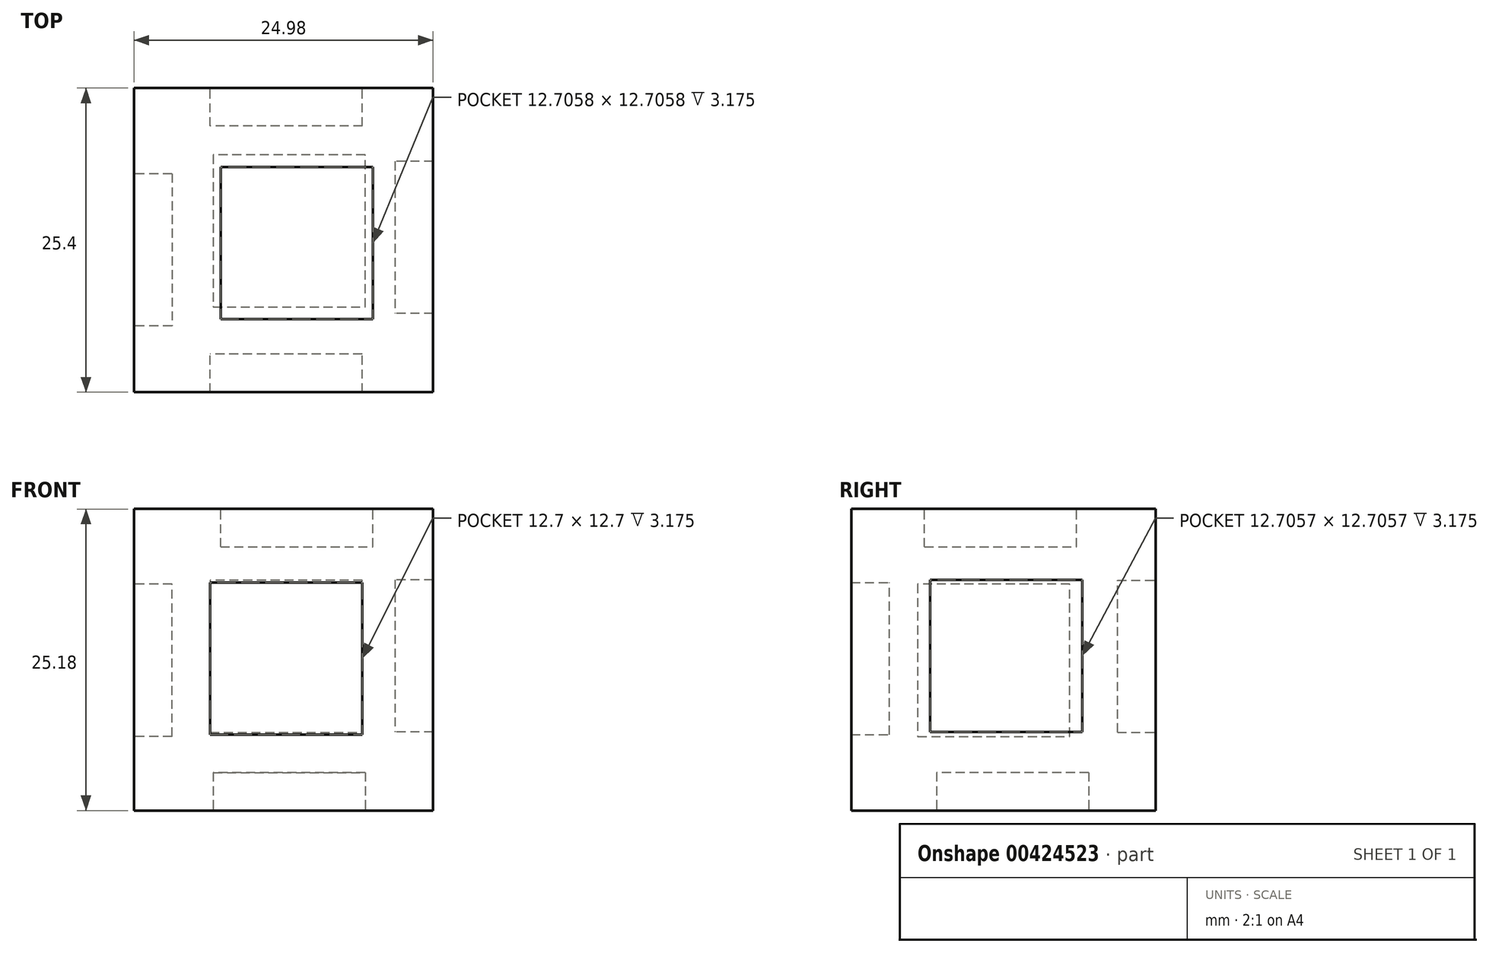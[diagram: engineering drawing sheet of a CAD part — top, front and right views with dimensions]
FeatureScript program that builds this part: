
annotation { "Feature Type Name" : "Feature", "Feature Type Description" : "" }
export const myFeature = defineFeature(function(context is Context, id is Id, definition is map)
    precondition{}
    {
        {
            var Q0;
            Q0=qCreatedBy(makeId("Front.planeOp"),FACE);
            var sketch = newSketch(context, id + "F0", { "sketchPlane" : qUnion([Q0])});
            skLineSegment(sketch, "E0", {"start": v(11.49, 11.84) * mm, "end": v(11.49, -13.56) * mm});
            skLineSegment(sketch, "E1", {"start": v(11.49, -13.56) * mm, "end": v(-13.49, -13.56) * mm});
            skLineSegment(sketch, "E2", {"start": v(-13.49, -13.56) * mm, "end": v(-13.49, 11.62) * mm});
            skLineSegment(sketch, "E3", {"start": v(-13.49, 11.62) * mm, "end": v(11.91, 11.62) * mm});
            skSolve(sketch);
        }
        {
            var Q0;
            Q0 = qSketchRegion(id + "F0", true);
            extrude(context, id + "F1", {"entities" : qUnion([Q0]), "depth" : 25.4 * mm});
        }
        {
            var Q0;
            Q0=makeQuery(id+"F1.opExtrude","CAP_FACE",FACE,{"disambiguationData":[OSD([sQuery(id+"F0.wireOp",EDGE,"E0"),sQuery(id+"F0.wireOp",EDGE,"E1"),sQuery(id+"F0.wireOp",EDGE,"E2"),sQuery(id+"F0.wireOp",EDGE,"E3")])],"isStart":false});
            var sketch = newSketch(context, id + "F2", { "sketchPlane" : qUnion([Q0])});
            skLineSegment(sketch, "E4", {"start": v(-7.14, 5.49) * mm, "end": v(5.56, 5.49) * mm});
            skLineSegment(sketch, "E5", {"start": v(5.56, 5.49) * mm, "end": v(5.56, -7.21) * mm});
            skLineSegment(sketch, "E6", {"start": v(5.56, -7.21) * mm, "end": v(-7.14, -7.21) * mm});
            skLineSegment(sketch, "E7", {"start": v(-7.14, -7.21) * mm, "end": v(-7.14, 5.49) * mm});
            skLineSegment(sketch, "E8", {"start": v(-7.14, 0) * mm, "end": v(-13.49, 0) * mm});
            skSolve(sketch);
        }
        {
            var Q0;
            {var subQ3=sQuery(id+"F2.wireOp",EDGE,"E4");Q0=makeQuery(id+"F2.imprint","IMPRINT",FACE,{"disambiguationData":[TD([[makeQuery(id+"F2.imprint","IMPRINT",EDGE,{"derivedFrom":subQ3}),-1.0]])]});}
            extrude(context, id + "F3", {"entities" : qUnion([Q0]), "operationType" : NewBodyOperationType.REMOVE, "oppositeDirection" : true, "depth" : 3.17 * mm});
        }
        {
            var Q0;
            Q0=makeQuery(id+"F1.opExtrude","SWEPT_FACE",FACE,{"disambiguationData":[OSD([sQuery(id+"F0.wireOp",EDGE,"E0")])]});
            var sketch = newSketch(context, id + "F4", { "sketchPlane" : qUnion([Q0])});
            skLineSegment(sketch, "E9", {"start": v(-6.12, 5.71) * mm, "end": v(-6.12, -7) * mm});
            skLineSegment(sketch, "E10", {"start": v(-6.12, -7) * mm, "end": v(-18.82, -7) * mm});
            skLineSegment(sketch, "E11", {"start": v(-18.82, -7) * mm, "end": v(-18.82, 5.71) * mm});
            skLineSegment(sketch, "E12", {"start": v(-6.12, 5.71) * mm, "end": v(-18.82, 5.71) * mm});
            skSolve(sketch);
        }
        {
            var Q0;
            Q0 = qSketchRegion(id + "F4", true);
            extrude(context, id + "F5", {"entities" : qUnion([Q0]), "operationType" : NewBodyOperationType.REMOVE, "oppositeDirection" : true, "depth" : 3.17 * mm});
        }
        {
            var Q0;
            Q0=makeQuery(id+"F1.opExtrude","SWEPT_FACE",FACE,{"disambiguationData":[OSD([sQuery(id+"F0.wireOp",EDGE,"E3")])]});
            var sketch = newSketch(context, id + "F6", { "sketchPlane" : qUnion([Q0])});
            skLineSegment(sketch, "E13", {"start": v(-6.25, -6.58) * mm, "end": v(6.45, -6.58) * mm});
            skLineSegment(sketch, "E14", {"start": v(6.45, -6.58) * mm, "end": v(6.45, -19.28) * mm});
            skLineSegment(sketch, "E15", {"start": v(6.45, -19.28) * mm, "end": v(-6.25, -19.28) * mm});
            skLineSegment(sketch, "E16", {"start": v(-6.25, -19.28) * mm, "end": v(-6.25, -6.58) * mm});
            skSolve(sketch);
        }
        {
            var Q0;
            Q0 = qSketchRegion(id + "F6", true);
            extrude(context, id + "F7", {"entities" : qUnion([Q0]), "operationType" : NewBodyOperationType.REMOVE, "oppositeDirection" : true, "depth" : 3.17 * mm});
        }
        {
            var Q0;
            Q0=makeQuery(id+"F1.opExtrude","CAP_FACE",FACE,{"disambiguationData":[OSD([sQuery(id+"F0.wireOp",EDGE,"E0"),sQuery(id+"F0.wireOp",EDGE,"E1"),sQuery(id+"F0.wireOp",EDGE,"E2"),sQuery(id+"F0.wireOp",EDGE,"E3")])],"isStart":true});
            var sketch = newSketch(context, id + "F8", { "sketchPlane" : qUnion([Q0])});
            skLineSegment(sketch, "E17", {"start": v(-5.58, 5.67) * mm, "end": v(7.12, 5.67) * mm});
            skLineSegment(sketch, "E18", {"start": v(7.12, 5.67) * mm, "end": v(7.12, -7.03) * mm});
            skLineSegment(sketch, "E19", {"start": v(7.12, -7.03) * mm, "end": v(-5.58, -7.03) * mm});
            skLineSegment(sketch, "E20", {"start": v(-5.58, -7.03) * mm, "end": v(-5.58, 5.67) * mm});
            skSolve(sketch);
        }
        {
            var Q0;
            Q0 = qSketchRegion(id + "F8", true);
            extrude(context, id + "F9", {"entities" : qUnion([Q0]), "operationType" : NewBodyOperationType.REMOVE, "oppositeDirection" : true, "depth" : 3.17 * mm});
        }
        {
            var Q0;
            Q0=makeQuery(id+"F1.opExtrude","SWEPT_FACE",FACE,{"disambiguationData":[OSD([sQuery(id+"F0.wireOp",EDGE,"E2")])]});
            var sketch = newSketch(context, id + "F10", { "sketchPlane" : qUnion([Q0])});
            skLineSegment(sketch, "E21", {"start": v(7.15, 5.34) * mm, "end": v(19.85, 5.34) * mm});
            skLineSegment(sketch, "E22", {"start": v(19.85, 5.34) * mm, "end": v(19.85, -7.37) * mm});
            skLineSegment(sketch, "E23", {"start": v(19.85, -7.37) * mm, "end": v(7.15, -7.37) * mm});
            skLineSegment(sketch, "E24", {"start": v(7.15, -7.37) * mm, "end": v(7.15, 5.34) * mm});
            skSolve(sketch);
        }
        {
            var Q0;
            Q0 = qSketchRegion(id + "F10", true);
            extrude(context, id + "F11", {"entities" : qUnion([Q0]), "operationType" : NewBodyOperationType.REMOVE, "oppositeDirection" : true, "depth" : 3.17 * mm});
        }
        {
            var Q0;
            Q0=makeQuery(id+"F1.opExtrude","SWEPT_FACE",FACE,{"disambiguationData":[OSD([sQuery(id+"F0.wireOp",EDGE,"E1")])]});
            var sketch = newSketch(context, id + "F12", { "sketchPlane" : qUnion([Q0])});
            skLineSegment(sketch, "E25", {"start": v(-6.86, 18.28) * mm, "end": v(5.83, 18.28) * mm});
            skLineSegment(sketch, "E26", {"start": v(5.83, 18.28) * mm, "end": v(5.83, 5.58) * mm});
            skLineSegment(sketch, "E27", {"start": v(5.83, 5.58) * mm, "end": v(-6.86, 5.58) * mm});
            skLineSegment(sketch, "E28", {"start": v(-6.86, 5.58) * mm, "end": v(-6.86, 18.28) * mm});
            skSolve(sketch);
        }
        {
            var Q0;
            Q0 = qSketchRegion(id + "F12", true);
            extrude(context, id + "F13", {"entities" : qUnion([Q0]), "operationType" : NewBodyOperationType.REMOVE, "oppositeDirection" : true, "depth" : 3.17 * mm});
        }
        {
            var Q0;
            Q0=makeQuery(id+"F3.boolean.opBoolean","COPY",FACE,{"derivedFrom":makeQuery(id+"F3.opExtrude","CAP_FACE",FACE,{"disambiguationData":[OSD([sQuery(id+"F2.wireOp",EDGE,"E4"),sQuery(id+"F2.wireOp",EDGE,"E5"),sQuery(id+"F2.wireOp",EDGE,"E6"),sQuery(id+"F2.wireOp",EDGE,"E7")])],"isStart":false})});
            var sketch = newSketch(context, id + "F14", { "sketchPlane" : qUnion([Q0])});
            skSolve(sketch);
        }
        {
            var Q0;
            Q0=makeQuery(id+"F14.imprint","IMPRINT",FACE,{"disambiguationData":[TD([[makeQuery(id+"F14.imprint","IMPRINT",EDGE,{"derivedFrom":makeQuery(id+"F3.boolean.opBoolean","COPY",EDGE,{"derivedFrom":makeQuery(id+"F3.opExtrude","CAP_EDGE",EDGE,{"disambiguationData":[OSD([sQuery(id+"F2.wireOp",EDGE,"E4")])],"isStart":false})})}),-1.0]])]});
            extrude(context, id + "F15", {"entities" : qUnion([Q0]), "depth" : 3.17 * mm});
        }
        {
            var Q0;
            Q0=makeQuery(id+"F5.boolean.opBoolean","COPY",FACE,{"derivedFrom":makeQuery(id+"F5.opExtrude","CAP_FACE",FACE,{"disambiguationData":[OSD([sQuery(id+"F4.wireOp",EDGE,"E9"),sQuery(id+"F4.wireOp",EDGE,"E10"),sQuery(id+"F4.wireOp",EDGE,"E11"),sQuery(id+"F4.wireOp",EDGE,"E12")])],"isStart":false})});
            var sketch = newSketch(context, id + "F16", { "sketchPlane" : qUnion([Q0])});
            skSolve(sketch);
        }
        {
            var Q0;
            Q0=makeQuery(id+"F16.imprint","IMPRINT",FACE,{"disambiguationData":[TD([[makeQuery(id+"F16.imprint","IMPRINT",EDGE,{"derivedFrom":makeQuery(id+"F5.boolean.opBoolean","COPY",EDGE,{"derivedFrom":makeQuery(id+"F5.opExtrude","CAP_EDGE",EDGE,{"disambiguationData":[OSD([sQuery(id+"F4.wireOp",EDGE,"E9")])],"isStart":false})})}),-1.0]])]});
            extrude(context, id + "F17", {"entities" : qUnion([Q0]), "depth" : 3.17 * mm});
        }
        {
            var Q0;
            Q0=makeQuery(id+"F7.boolean.opBoolean","COPY",FACE,{"derivedFrom":makeQuery(id+"F7.opExtrude","CAP_FACE",FACE,{"disambiguationData":[OSD([sQuery(id+"F6.wireOp",EDGE,"E13"),sQuery(id+"F6.wireOp",EDGE,"E14"),sQuery(id+"F6.wireOp",EDGE,"E15"),sQuery(id+"F6.wireOp",EDGE,"E16")])],"isStart":false})});
            var sketch = newSketch(context, id + "F18", { "sketchPlane" : qUnion([Q0])});
            skSolve(sketch);
        }
        {
            var Q0;
            Q0=makeQuery(id+"F18.imprint","IMPRINT",FACE,{"disambiguationData":[TD([[makeQuery(id+"F18.imprint","IMPRINT",EDGE,{"derivedFrom":makeQuery(id+"F7.boolean.opBoolean","COPY",EDGE,{"derivedFrom":makeQuery(id+"F7.opExtrude","CAP_EDGE",EDGE,{"disambiguationData":[OSD([sQuery(id+"F6.wireOp",EDGE,"E13")])],"isStart":false})})}),-1.0]])]});
            extrude(context, id + "F19", {"entities" : qUnion([Q0]), "depth" : 3.17 * mm});
        }
        {
            var Q0;
            Q0=makeQuery(id+"F9.boolean.opBoolean","COPY",FACE,{"derivedFrom":makeQuery(id+"F9.opExtrude","CAP_FACE",FACE,{"disambiguationData":[OSD([sQuery(id+"F8.wireOp",EDGE,"E17"),sQuery(id+"F8.wireOp",EDGE,"E18"),sQuery(id+"F8.wireOp",EDGE,"E19"),sQuery(id+"F8.wireOp",EDGE,"E20")])],"isStart":false})});
            extrude(context, id + "F20", {"entities" : qUnion([Q0]), "depth" : 3.17 * mm});
        }
        {
            var Q0;
            Q0=makeQuery(id+"F11.boolean.opBoolean","COPY",FACE,{"derivedFrom":makeQuery(id+"F11.opExtrude","CAP_FACE",FACE,{"disambiguationData":[OSD([sQuery(id+"F10.wireOp",EDGE,"E21"),sQuery(id+"F10.wireOp",EDGE,"E22"),sQuery(id+"F10.wireOp",EDGE,"E23"),sQuery(id+"F10.wireOp",EDGE,"E24")])],"isStart":false})});
            var sketch = newSketch(context, id + "F21", { "sketchPlane" : qUnion([Q0])});
            skSolve(sketch);
        }
        {
            var Q0;
            Q0=makeQuery(id+"F21.imprint","IMPRINT",FACE,{"disambiguationData":[TD([[makeQuery(id+"F21.imprint","IMPRINT",EDGE,{"derivedFrom":makeQuery(id+"F11.boolean.opBoolean","COPY",EDGE,{"derivedFrom":makeQuery(id+"F11.opExtrude","CAP_EDGE",EDGE,{"disambiguationData":[OSD([sQuery(id+"F10.wireOp",EDGE,"E21")])],"isStart":false})})}),-1.0]])]});
            extrude(context, id + "F22", {"entities" : qUnion([Q0]), "depth" : 3.17 * mm});
        }
        {
            var Q0;
            Q0=makeQuery(id+"F13.boolean.opBoolean","COPY",FACE,{"derivedFrom":makeQuery(id+"F13.opExtrude","CAP_FACE",FACE,{"disambiguationData":[OSD([sQuery(id+"F12.wireOp",EDGE,"E25"),sQuery(id+"F12.wireOp",EDGE,"E26"),sQuery(id+"F12.wireOp",EDGE,"E27"),sQuery(id+"F12.wireOp",EDGE,"E28")])],"isStart":false})});
            var sketch = newSketch(context, id + "F23", { "sketchPlane" : qUnion([Q0])});
            skSolve(sketch);
        }
        {
            var Q0;
            Q0=makeQuery(id+"F23.imprint","IMPRINT",FACE,{"disambiguationData":[TD([[makeQuery(id+"F23.imprint","IMPRINT",EDGE,{"derivedFrom":makeQuery(id+"F13.boolean.opBoolean","COPY",EDGE,{"derivedFrom":makeQuery(id+"F13.opExtrude","CAP_EDGE",EDGE,{"disambiguationData":[OSD([sQuery(id+"F12.wireOp",EDGE,"E25")])],"isStart":false})})}),-1.0]])]});
            extrude(context, id + "F24", {"entities" : qUnion([Q0]), "depth" : 3.17 * mm});
        }
    });
